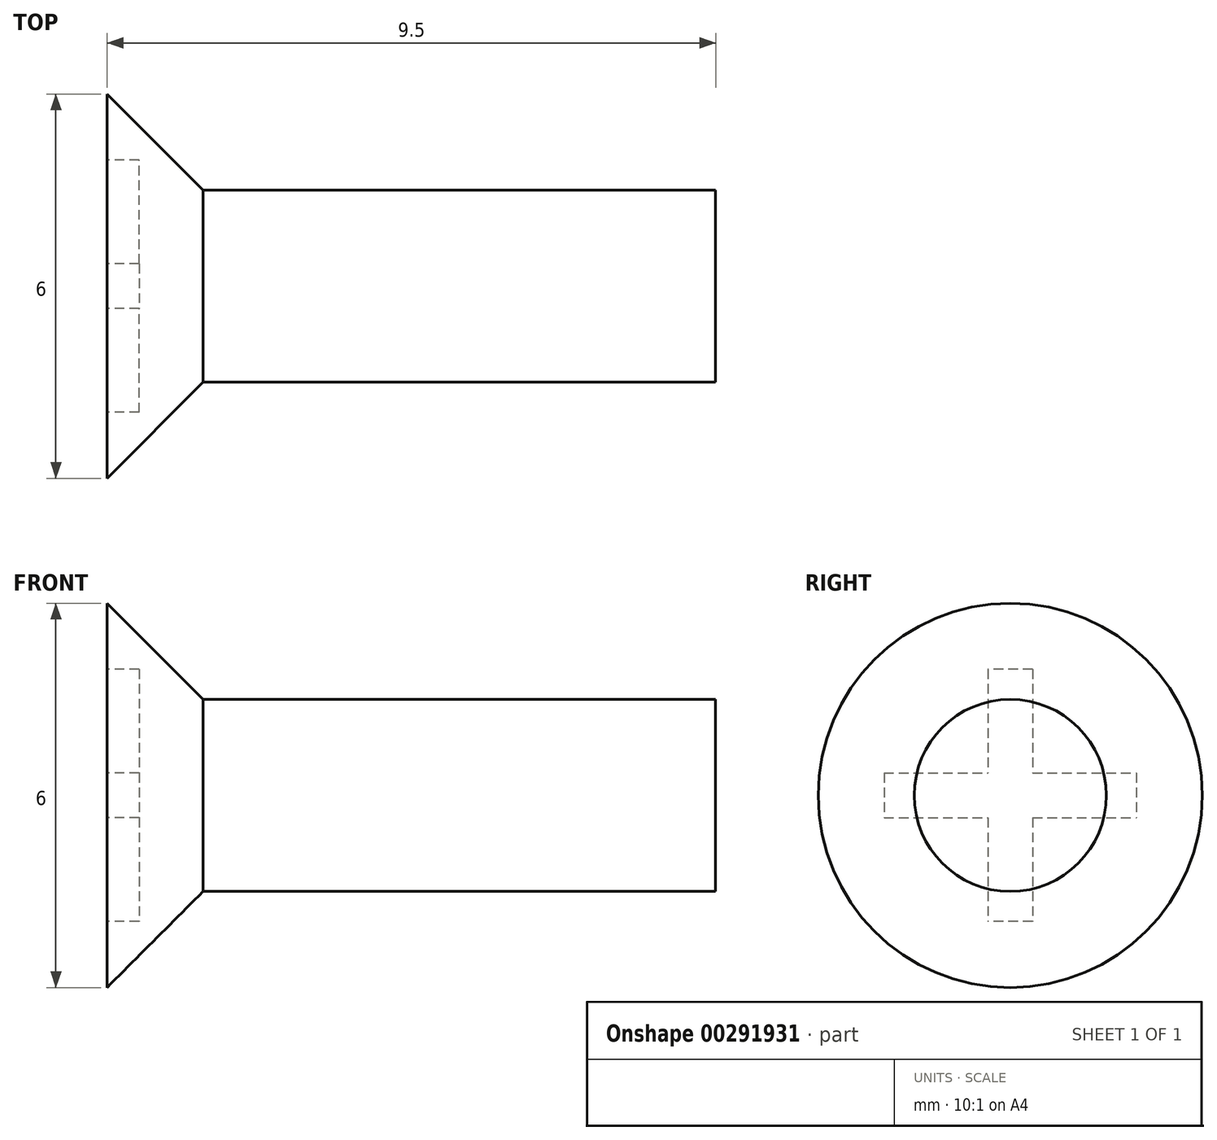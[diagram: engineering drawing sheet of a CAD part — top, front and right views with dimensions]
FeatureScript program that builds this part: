
annotation { "Feature Type Name" : "Feature", "Feature Type Description" : "" }
export const myFeature = defineFeature(function(context is Context, id is Id, definition is map)
    precondition{}
    {
        {
            var Q0;
            Q0=qCreatedBy(makeId("Front.planeOp"),FACE);
            var sketch = newSketch(context, id + "F0", { "sketchPlane" : qUnion([Q0])});
            skLineSegment(sketch, "E0", {"start": v(-6.27, 0) * mm, "end": v(-6.27, 3) * mm});
            skLineSegment(sketch, "E1", {"start": v(-6.27, 3) * mm, "end": v(-4.77, 1.5) * mm});
            skLineSegment(sketch, "E2", {"start": v(-4.77, 1.5) * mm, "end": v(3.23, 1.5) * mm});
            skLineSegment(sketch, "E3", {"start": v(3.23, 1.5) * mm, "end": v(3.23, 0) * mm});
            skLineSegment(sketch, "E4", {"start": v(3.23, 0) * mm, "end": v(-9.17, 0) * mm, "construction": true});
            skLineSegment(sketch, "E5", {"start": v(-6.27, 0) * mm, "end": v(3.23, 0) * mm});
            skSolve(sketch);
        }
        {
            var Q0;
            Q0=makeQuery(id+"F0.imprint","IMPRINT",FACE,{"disambiguationData":[TD([[makeQuery(id+"F0.imprint","IMPRINT",EDGE,{"derivedFrom":sQuery(id+"F0.wireOp",EDGE,"E0")}),-1.0]])]});
            var Q1;
            Q1=sQuery(id+"F0.wireOp",EDGE,"E4");
            revolve(context, id + "F1", {"entities" : qUnion([Q0]), "axis" : qUnion([Q1]), "revolveType" : RevolveType.FULL});
        }
        {
            var Q0;
            Q0=makeQuery(id+"F1.opRevolve","SWEPT_FACE",FACE,{"disambiguationData":[OSD([sQuery(id+"F0.wireOp",EDGE,"E0")])]});
            var sketch = newSketch(context, id + "F2", { "sketchPlane" : qUnion([Q0])});
            skCircle(sketch, "E6", {"center": v(0, 0) * mm, "radius": 2 * mm});
            skLineSegment(sketch, "E7.bottom", {"start": v(-0.35, 1.97) * mm, "end": v(0.35, 1.97) * mm});
            skLineSegment(sketch, "E7.top", {"start": v(-0.35, -1.97) * mm, "end": v(0.35, -1.97) * mm});
            skLineSegment(sketch, "E7.left", {"start": v(-0.35, 1.97) * mm, "end": v(-0.35, -1.97) * mm});
            skLineSegment(sketch, "E7.right", {"start": v(0.35, 1.97) * mm, "end": v(0.35, -1.97) * mm});
            skLineSegment(sketch, "E8.1.0", {"start": v(1.97, 0.35) * mm, "end": v(-1.97, 0.35) * mm});
            skLineSegment(sketch, "E8.1.1", {"start": v(1.97, -0.35) * mm, "end": v(-1.97, -0.35) * mm});
            skLineSegment(sketch, "E8.1.2", {"start": v(1.97, 0.35) * mm, "end": v(1.97, -0.35) * mm});
            skLineSegment(sketch, "E8.1.3", {"start": v(-1.97, 0.35) * mm, "end": v(-1.97, -0.35) * mm});
            skLineSegment(sketch, "E8.anchor1", {"start": v(0, 0) * mm, "end": v(-0.35, -1.97) * mm, "construction": true});
            skLineSegment(sketch, "E8.anchor2", {"start": v(0, 0) * mm, "end": v(-1.97, 0.35) * mm, "construction": true});
            skSolve(sketch);
        }
        {
            var Q0;
            {var subQ5=sQuery(id+"F2.wireOp",EDGE,"E8.1.3");Q0=makeQuery(id+"F2.imprint","IMPRINT",FACE,{"disambiguationData":[TD([[makeQuery(id+"F2.imprint","IMPRINT",EDGE,{"derivedFrom":subQ5}),1.0]])]});}
            var Q1;
            {var subQ0=sQuery(id+"F2.wireOp",EDGE,"E7.bottom");Q1=makeQuery(id+"F2.imprint","IMPRINT",FACE,{"disambiguationData":[TD([[makeQuery(id+"F2.imprint","IMPRINT",EDGE,{"derivedFrom":subQ0}),-1.0]])]});}
            var Q2;
            {var subQ0=sQuery(id+"F2.wireOp",EDGE,"E8.1.0");var subQ1=sQuery(id+"F2.wireOp",EDGE,"E7.left");var subQ2=makeQuery(id+"F2.imprint","INTERSECT",VERTEX,{"derivedFrom":[subQ1,subQ0]});Q2=makeQuery(id+"F2.imprint","IMPRINT",FACE,{"disambiguationData":[TD([[makeQuery(id+"F2.imprint","IMPRINT",EDGE,{"disambiguationData":[TD([[subQ2,-1.0]])],"derivedFrom":subQ1}),1.0]])]});}
            var Q3;
            {var subQ5=sQuery(id+"F2.wireOp",EDGE,"E8.1.2");Q3=makeQuery(id+"F2.imprint","IMPRINT",FACE,{"disambiguationData":[TD([[makeQuery(id+"F2.imprint","IMPRINT",EDGE,{"derivedFrom":subQ5}),-1.0]])]});}
            var Q4;
            {var subQ0=sQuery(id+"F2.wireOp",EDGE,"E7.top");Q4=makeQuery(id+"F2.imprint","IMPRINT",FACE,{"disambiguationData":[TD([[makeQuery(id+"F2.imprint","IMPRINT",EDGE,{"derivedFrom":subQ0}),1.0]])]});}
            extrude(context, id + "F3", {"entities" : qUnion([Q0, Q1, Q2, Q3, Q4]), "operationType" : NewBodyOperationType.REMOVE, "oppositeDirection" : true, "depth" : 0.5 * mm});
        }
    });
